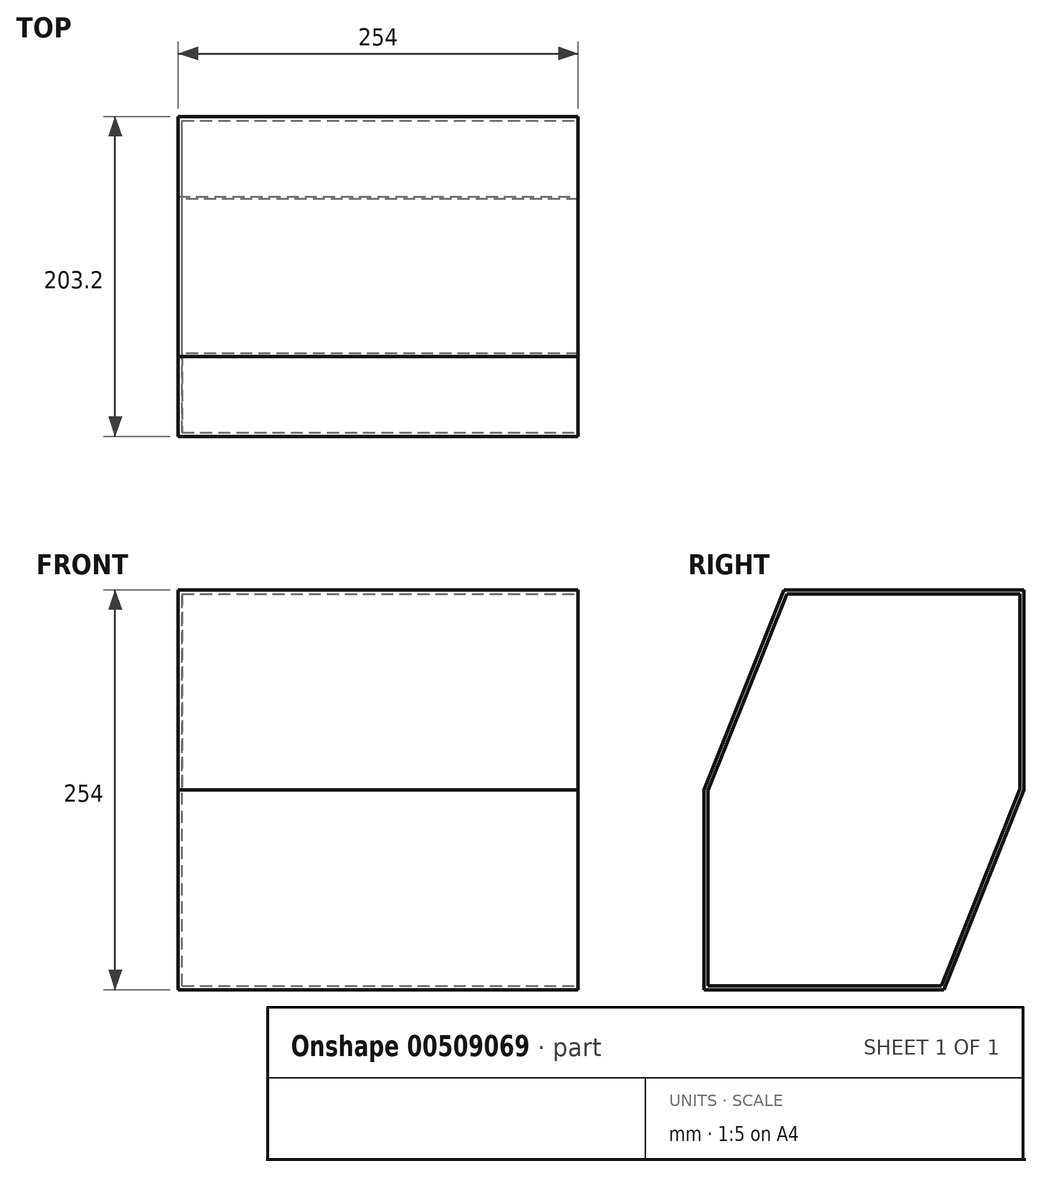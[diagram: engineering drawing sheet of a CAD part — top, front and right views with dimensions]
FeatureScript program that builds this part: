
annotation { "Feature Type Name" : "Feature", "Feature Type Description" : "" }
export const myFeature = defineFeature(function(context is Context, id is Id, definition is map)
    precondition{}
    {
        {
            var Q0;
            Q0=qCreatedBy(makeId("Front.planeOp"),FACE);
            var sketch = newSketch(context, id + "F0", { "sketchPlane" : qUnion([Q0])});
            skLineSegment(sketch, "E0.bottom", {"start": v(0, 0) * mm, "end": v(254, 0) * mm});
            skLineSegment(sketch, "E0.top", {"start": v(0, 254) * mm, "end": v(254, 254) * mm});
            skLineSegment(sketch, "E0.left", {"start": v(0, 0) * mm, "end": v(0, 254) * mm});
            skLineSegment(sketch, "E0.right", {"start": v(254, 0) * mm, "end": v(254, 254) * mm});
            skSolve(sketch);
        }
        {
            var Q0;
            Q0=makeQuery(id+"F0.imprint","IMPRINT",FACE,{"disambiguationData":[TD([[makeQuery(id+"F0.imprint","IMPRINT",EDGE,{"derivedFrom":sQuery(id+"F0.wireOp",EDGE,"E0.bottom")}),1.0]])]});
            extrude(context, id + "F1", {"entities" : qUnion([Q0]), "depth" : 203.2 * mm});
        }
        {
            var Q0;
            Q0=makeQuery(id+"F1.opExtrude","CAP_EDGE",EDGE,{"disambiguationData":[OSD([sQuery(id+"F0.wireOp",EDGE,"E0.top")])],"isStart":false});
            var Q1;
            Q1=makeQuery(id+"F1.opExtrude","CAP_EDGE",EDGE,{"disambiguationData":[OSD([sQuery(id+"F0.wireOp",EDGE,"E0.bottom")])],"isStart":true});
            chamfer(context, id + "F2", {"entities" : qUnion([Q0, Q1]), "chamferType" : ChamferType.TWO_OFFSETS, "width1" : 50.8 * mm, "oppositeDirection" : false, "width2" : 127 * mm, "tangentPropagation" : true});
        }
        {
            var Q0;
            Q0=makeQuery(id+"F1.opExtrude","SWEPT_FACE",FACE,{"disambiguationData":[OSD([sQuery(id+"F0.wireOp",EDGE,"E0.right")])]});
            shell(context, id + "F3", {"entities" : qUnion([Q0]), "thickness" : 2.54 * mm});
        }
    });
